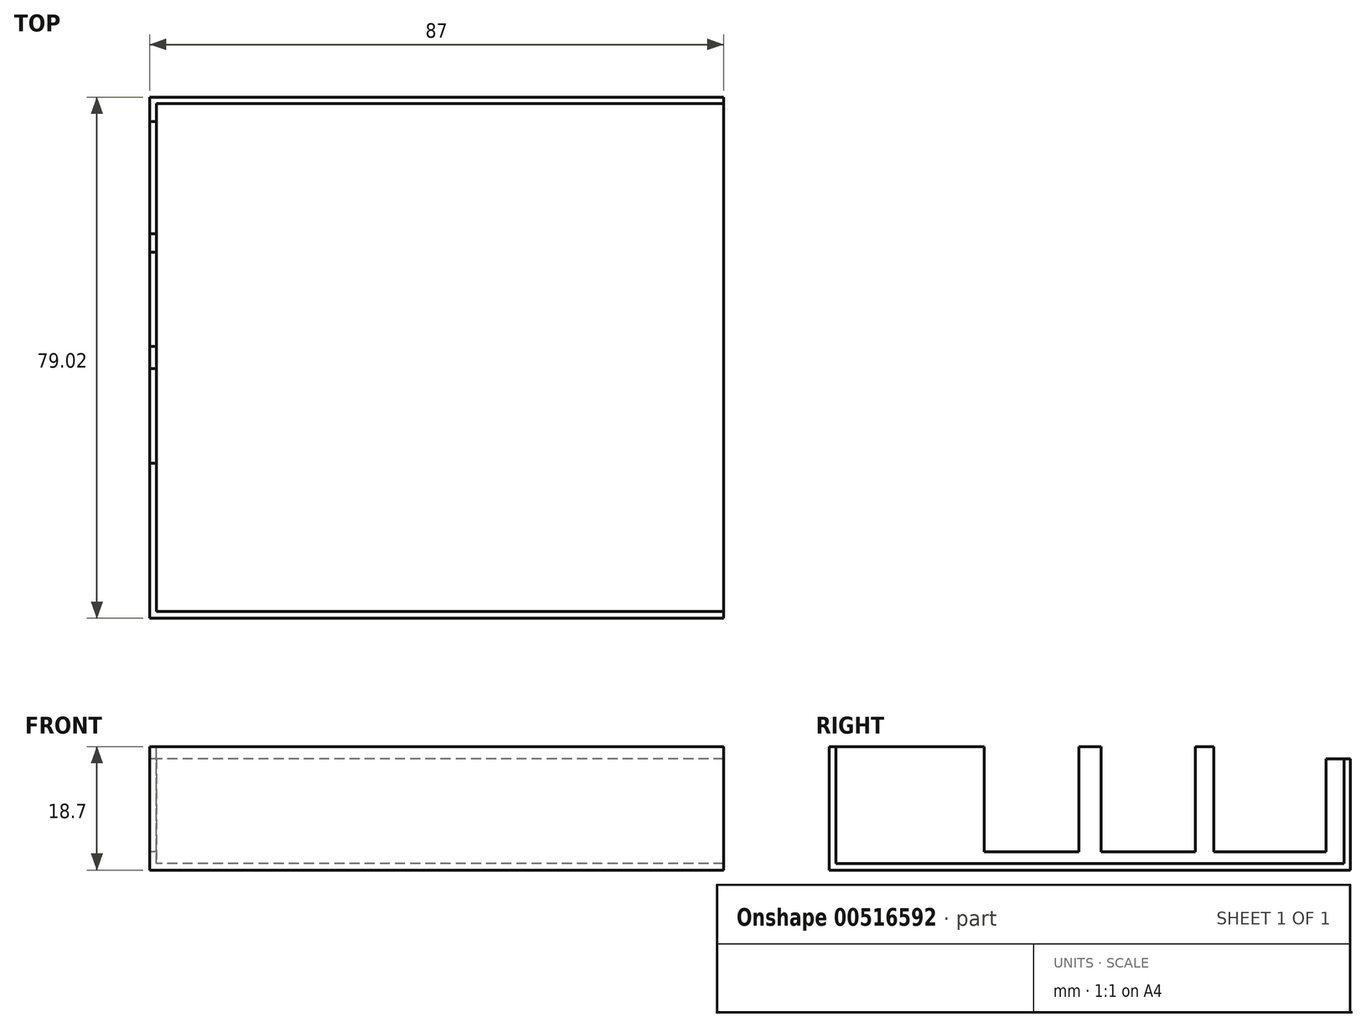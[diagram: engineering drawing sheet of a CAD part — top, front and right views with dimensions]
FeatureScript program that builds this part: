
annotation { "Feature Type Name" : "Feature", "Feature Type Description" : "" }
export const myFeature = defineFeature(function(context is Context, id is Id, definition is map)
    precondition{}
    {
        {
            var Q0;
            Q0=qCreatedBy(makeId("Right.planeOp"),FACE);
            var sketch = newSketch(context, id + "F0", { "sketchPlane" : qUnion([Q0])});
            skLineSegment(sketch, "E0", {"start": v(58, -3.3) * mm, "end": v(-21.02, -3.3) * mm});
            skLineSegment(sketch, "E1", {"start": v(58, -3.3) * mm, "end": v(58, 13.6) * mm});
            skLineSegment(sketch, "E2", {"start": v(58, 13.6) * mm, "end": v(54.3, 13.6) * mm});
            skLineSegment(sketch, "E3", {"start": v(54.3, 13.6) * mm, "end": v(54.3, -0.5) * mm});
            skLineSegment(sketch, "E4", {"start": v(54.3, -0.5) * mm, "end": v(37.3, -0.5) * mm});
            skLineSegment(sketch, "E5", {"start": v(37.3, -0.5) * mm, "end": v(37.3, 15.4) * mm});
            skLineSegment(sketch, "E6", {"start": v(37.3, 15.4) * mm, "end": v(34.5, 15.4) * mm});
            skLineSegment(sketch, "E7", {"start": v(34.5, 15.4) * mm, "end": v(34.5, -0.5) * mm});
            skLineSegment(sketch, "E8", {"start": v(34.5, -0.5) * mm, "end": v(20.2, -0.5) * mm});
            skLineSegment(sketch, "E9", {"start": v(20.2, -0.5) * mm, "end": v(20.2, 15.4) * mm});
            skLineSegment(sketch, "E10", {"start": v(2.5, 15.4) * mm, "end": v(-21.02, 15.4) * mm});
            skLineSegment(sketch, "E11", {"start": v(-21.02, 15.4) * mm, "end": v(-21.02, -3.3) * mm});
            skLineSegment(sketch, "E12", {"start": v(20.2, 15.4) * mm, "end": v(16.8, 15.4) * mm});
            skLineSegment(sketch, "E13", {"start": v(16.8, 15.4) * mm, "end": v(16.8, -0.5) * mm});
            skLineSegment(sketch, "E14", {"start": v(16.8, -0.5) * mm, "end": v(2.5, -0.5) * mm});
            skLineSegment(sketch, "E15", {"start": v(2.5, -0.5) * mm, "end": v(2.5, 15.4) * mm});
            skPoint(sketch, "E16", {"position": v(0, 0) * mm});
            skSolve(sketch);
        }
        {
            var Q0;
            Q0 = qSketchRegion(id + "F0", true);
            extrude(context, id + "F1", {"entities" : qUnion([Q0]), "depth" : 1 * mm, "offsetDistance" : 25 * mm});
        }
        {
            var Q0;
            Q0=makeQuery(id+"F1.opExtrude","CAP_FACE",FACE,{"disambiguationData":[OSD([sQuery(id+"F0.wireOp",EDGE,"E0"),sQuery(id+"F0.wireOp",EDGE,"E1"),sQuery(id+"F0.wireOp",EDGE,"E2"),sQuery(id+"F0.wireOp",EDGE,"E3"),sQuery(id+"F0.wireOp",EDGE,"E4"),sQuery(id+"F0.wireOp",EDGE,"E5"),sQuery(id+"F0.wireOp",EDGE,"E6"),sQuery(id+"F0.wireOp",EDGE,"E7"),sQuery(id+"F0.wireOp",EDGE,"E8"),sQuery(id+"F0.wireOp",EDGE,"E9"),sQuery(id+"F0.wireOp",EDGE,"E10"),sQuery(id+"F0.wireOp",EDGE,"E11"),sQuery(id+"F0.wireOp",EDGE,"E12"),sQuery(id+"F0.wireOp",EDGE,"E13"),sQuery(id+"F0.wireOp",EDGE,"E14"),sQuery(id+"F0.wireOp",EDGE,"E15")])],"isStart":false});
            var sketch = newSketch(context, id + "F2", { "sketchPlane" : qUnion([Q0])});
            skLineSegment(sketch, "E17", {"start": v(-21.02, 15.4) * mm, "end": v(-21.02, -3.3) * mm});
            skLineSegment(sketch, "E18", {"start": v(-21.02, -3.3) * mm, "end": v(58, -3.3) * mm});
            skLineSegment(sketch, "E19", {"start": v(58, -3.3) * mm, "end": v(58, 13.6) * mm});
            skLineSegment(sketch, "E20", {"start": v(58, 13.6) * mm, "end": v(57, 13.6) * mm});
            skLineSegment(sketch, "E21", {"start": v(57, 13.6) * mm, "end": v(57, -2.3) * mm});
            skLineSegment(sketch, "E22", {"start": v(57, -2.3) * mm, "end": v(-20.02, -2.3) * mm});
            skLineSegment(sketch, "E23", {"start": v(-20.02, -2.3) * mm, "end": v(-20.02, 15.4) * mm});
            skLineSegment(sketch, "E24", {"start": v(-20.02, 15.4) * mm, "end": v(-21.02, 15.4) * mm});
            skSolve(sketch);
        }
        {
            var Q0;
            Q0 = qSketchRegion(id + "F2", true);
            extrude(context, id + "F3", {"entities" : qUnion([Q0]), "operationType" : NewBodyOperationType.ADD, "depth" : 86 * mm, "offsetDistance" : 25 * mm});
        }
    });
